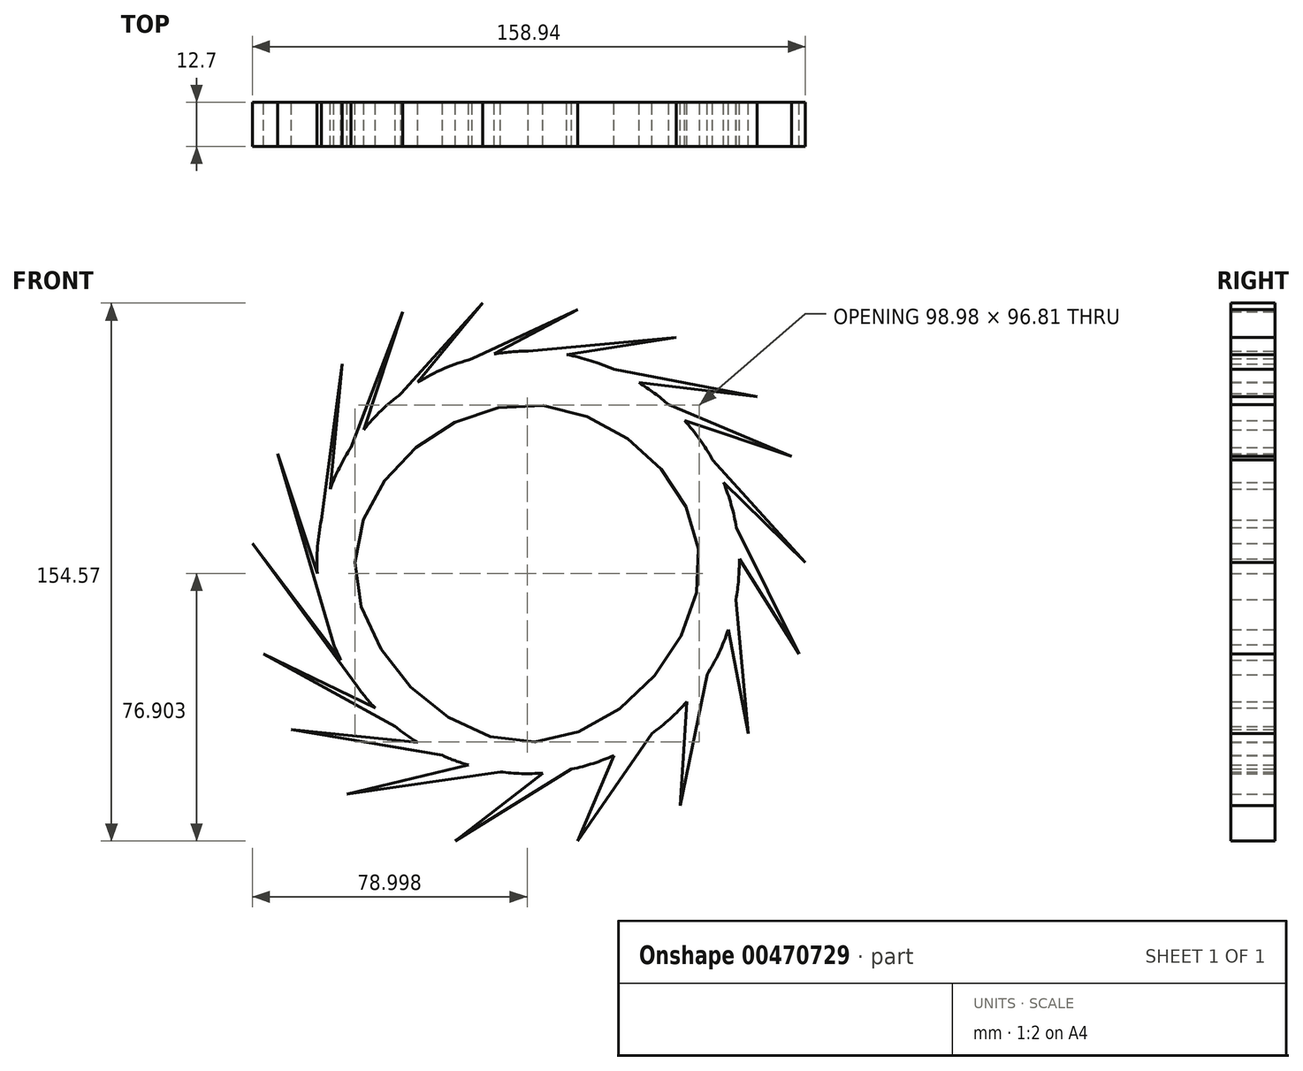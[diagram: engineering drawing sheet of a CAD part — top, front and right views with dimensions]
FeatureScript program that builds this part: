
annotation { "Feature Type Name" : "Feature", "Feature Type Description" : "" }
export const myFeature = defineFeature(function(context is Context, id is Id, definition is map)
    precondition{}
    {
        {
            var Q0;
            Q0=qCreatedBy(makeId("Front.planeOp"),FACE);
            var sketch = newSketch(context, id + "F0", { "sketchPlane" : qUnion([Q0])});
            skArc(sketch, "E0", {"start": v(-16.12, 58.5) * mm, "mid": v(-24.14, 55.68) * mm, "end": v(-31.68, 51.76) * mm});
            skLineSegment(sketch, "E1", {"start": v(-59.45, 12.2) * mm, "end": v(-53.45, 57.05) * mm});
            skLineSegment(sketch, "E2", {"start": v(-53.45, 57.05) * mm, "end": v(-56.92, 21.05) * mm});
            skLineSegment(sketch, "E3", {"start": v(-50.89, 33.06) * mm, "end": v(-36, 71.96) * mm});
            skLineSegment(sketch, "E4", {"start": v(-36, 71.96) * mm, "end": v(-47.22, 38.12) * mm});
            skLineSegment(sketch, "E5", {"start": v(-36.49, 48.5) * mm, "end": v(-13.08, 74.5) * mm});
            skLineSegment(sketch, "E6", {"start": v(-13.08, 74.5) * mm, "end": v(-31.68, 51.76) * mm});
            skLineSegment(sketch, "E7", {"start": v(-16.12, 58.5) * mm, "end": v(14.2, 72.69) * mm});
            skLineSegment(sketch, "E8", {"start": v(14.2, 72.69) * mm, "end": v(-9.8, 59.9) * mm});
            skArc(sketch, "E9.trimOffspring", {"start": v(-36.49, 48.5) * mm, "mid": v(-42.17, 43.64) * mm, "end": v(-47.22, 38.12) * mm});
            skArc(sketch, "E10.trimOffspring", {"start": v(-50.89, 33.06) * mm, "mid": v(-54.24, 27.23) * mm, "end": v(-56.92, 21.05) * mm});
            skArc(sketch, "E11.trimOffspring", {"start": v(-59.45, 12.2) * mm, "mid": v(-60.51, 4.55) * mm, "end": v(-60.6, -3.17) * mm});
            skArc(sketch, "E12.trimOffspring", {"start": v(-55.87, -23.69) * mm, "mid": v(-54.89, -25.89) * mm, "end": v(-53.82, -28.04) * mm});
            skLineSegment(sketch, "E13", {"start": v(0, 60.69) * mm, "end": v(42.56, 64.68) * mm});
            skLineSegment(sketch, "E14", {"start": v(42.56, 64.68) * mm, "end": v(11.13, 59.66) * mm});
            skLineSegment(sketch, "E15", {"start": v(24.64, 55.46) * mm, "end": v(65.84, 47.6) * mm});
            skLineSegment(sketch, "E16", {"start": v(65.84, 47.6) * mm, "end": v(31.86, 51.65) * mm});
            skLineSegment(sketch, "E17", {"start": v(40.42, 45.27) * mm, "end": v(75.66, 30.5) * mm});
            skLineSegment(sketch, "E18", {"start": v(75.66, 30.5) * mm, "end": v(44.98, 40.74) * mm});
            skLineSegment(sketch, "E19", {"start": v(53.04, 29.48) * mm, "end": v(79.66, 0) * mm});
            skLineSegment(sketch, "E20", {"start": v(79.66, 0) * mm, "end": v(56.18, 22.95) * mm});
            skArc(sketch, "E21.trimOffspring", {"start": v(24.64, 55.46) * mm, "mid": v(18, 57.95) * mm, "end": v(11.13, 59.66) * mm});
            skArc(sketch, "E22.trimOffspring", {"start": v(0, 60.69) * mm, "mid": v(-4.91, 60.49) * mm, "end": v(-9.8, 59.9) * mm});
            skArc(sketch, "E23.trimOffspring", {"start": v(40.42, 45.27) * mm, "mid": v(36.28, 48.65) * mm, "end": v(31.86, 51.65) * mm});
            skArc(sketch, "E24.trimOffspring", {"start": v(53.04, 29.48) * mm, "mid": v(49.33, 35.34) * mm, "end": v(44.98, 40.74) * mm});
            skLineSegment(sketch, "E25", {"start": v(59.74, -10.68) * mm, "end": v(63.3, -49.16) * mm});
            skLineSegment(sketch, "E26", {"start": v(63.3, -49.16) * mm, "end": v(57.52, -19.33) * mm});
            skArc(sketch, "E27.trimOffspring", {"start": v(59.86, 9.96) * mm, "mid": v(58.38, 16.56) * mm, "end": v(56.18, 22.95) * mm});
            skArc(sketch, "E28.trimOffspring", {"start": v(59.74, -10.68) * mm, "mid": v(60.49, -4.88) * mm, "end": v(60.68, 0.96) * mm});
            skLineSegment(sketch, "E29", {"start": v(51.43, -32.2) * mm, "end": v(43.66, -69.89) * mm});
            skLineSegment(sketch, "E30", {"start": v(43.66, -69.89) * mm, "end": v(45.58, -40.06) * mm});
            skArc(sketch, "E31.trimOffspring", {"start": v(51.43, -32.2) * mm, "mid": v(54.86, -25.95) * mm, "end": v(57.52, -19.33) * mm});
            skLineSegment(sketch, "E32", {"start": v(-60.6, -3.17) * mm, "end": v(-72, 31.22) * mm});
            skLineSegment(sketch, "E33", {"start": v(-72, 31.22) * mm, "end": v(-55.87, -23.69) * mm});
            skLineSegment(sketch, "E34", {"start": v(60.68, 0.96) * mm, "end": v(77.84, -26.24) * mm});
            skLineSegment(sketch, "E35", {"start": v(77.84, -26.24) * mm, "end": v(59.86, 9.96) * mm});
            skLineSegment(sketch, "E36", {"start": v(35.53, -49.2) * mm, "end": v(14.2, -80.07) * mm});
            skLineSegment(sketch, "E37", {"start": v(14.2, -80.07) * mm, "end": v(24.61, -55.47) * mm});
            skArc(sketch, "E38.trimOffspring", {"start": v(35.53, -49.2) * mm, "mid": v(40.81, -44.91) * mm, "end": v(45.58, -40.06) * mm});
            skLineSegment(sketch, "E39", {"start": v(12.52, -59.38) * mm, "end": v(-20.98, -80.07) * mm});
            skLineSegment(sketch, "E40", {"start": v(-20.98, -80.07) * mm, "end": v(4.26, -60.54) * mm});
            skArc(sketch, "E41.trimOffspring", {"start": v(12.52, -59.38) * mm, "mid": v(18.67, -57.74) * mm, "end": v(24.61, -55.47) * mm});
            skLineSegment(sketch, "E42", {"start": v(-7.91, -60.17) * mm, "end": v(-52, -66.61) * mm});
            skLineSegment(sketch, "E43", {"start": v(-52, -66.61) * mm, "end": v(-17.17, -58.2) * mm});
            skLineSegment(sketch, "E44", {"start": v(-24.67, -55.45) * mm, "end": v(-68, -48.06) * mm});
            skLineSegment(sketch, "E45", {"start": v(-68, -48.06) * mm, "end": v(-31.7, -51.74) * mm});
            skLineSegment(sketch, "E46", {"start": v(-38.23, -47.13) * mm, "end": v(-76, -26.24) * mm});
            skLineSegment(sketch, "E47", {"start": v(-76, -26.24) * mm, "end": v(-43.95, -41.84) * mm});
            skLineSegment(sketch, "E48", {"start": v(-48.65, -36.27) * mm, "end": v(-79.28, 5.4) * mm});
            skLineSegment(sketch, "E49", {"start": v(-79.28, 5.4) * mm, "end": v(-53.82, -28.04) * mm});
            skArc(sketch, "E50.trimOffspring", {"start": v(-7.91, -60.17) * mm, "mid": v(-1.83, -60.66) * mm, "end": v(4.26, -60.54) * mm});
            skArc(sketch, "E51.trimOffspring", {"start": v(-24.67, -55.45) * mm, "mid": v(-20.96, -56.95) * mm, "end": v(-17.17, -58.2) * mm});
            skArc(sketch, "E52.trimOffspring", {"start": v(-38.23, -47.13) * mm, "mid": v(-35.04, -49.54) * mm, "end": v(-31.7, -51.74) * mm});
            skArc(sketch, "E53.trimOffspring", {"start": v(-49.15, -35.6) * mm, "mid": v(-46.65, -38.8) * mm, "end": v(-43.95, -41.84) * mm});
            skSolve(sketch);
        }
        {
            var Q0;
            Q0 = qSketchRegion(id + "F0", true);
            extrude(context, id + "F1", {"entities" : qUnion([Q0]), "depth" : 12.7 * mm});
        }
        {
            var Q0;
            Q0=makeQuery(id+"F1.opExtrude","CAP_FACE",FACE,{"disambiguationData":[OSD([sQuery(id+"F0.wireOp",EDGE,"E0"),sQuery(id+"F0.wireOp",EDGE,"E1"),sQuery(id+"F0.wireOp",EDGE,"E2"),sQuery(id+"F0.wireOp",EDGE,"E3"),sQuery(id+"F0.wireOp",EDGE,"E4"),sQuery(id+"F0.wireOp",EDGE,"E5"),sQuery(id+"F0.wireOp",EDGE,"E6"),sQuery(id+"F0.wireOp",EDGE,"E7"),sQuery(id+"F0.wireOp",EDGE,"E8"),sQuery(id+"F0.wireOp",EDGE,"E9.trimOffspring"),sQuery(id+"F0.wireOp",EDGE,"E10.trimOffspring"),sQuery(id+"F0.wireOp",EDGE,"E11.trimOffspring"),sQuery(id+"F0.wireOp",EDGE,"E12.trimOffspring"),sQuery(id+"F0.wireOp",EDGE,"E13"),sQuery(id+"F0.wireOp",EDGE,"E14"),sQuery(id+"F0.wireOp",EDGE,"E15"),sQuery(id+"F0.wireOp",EDGE,"E16"),sQuery(id+"F0.wireOp",EDGE,"E17"),sQuery(id+"F0.wireOp",EDGE,"E18"),sQuery(id+"F0.wireOp",EDGE,"E19"),sQuery(id+"F0.wireOp",EDGE,"E20"),sQuery(id+"F0.wireOp",EDGE,"E21.trimOffspring"),sQuery(id+"F0.wireOp",EDGE,"E22.trimOffspring"),sQuery(id+"F0.wireOp",EDGE,"E23.trimOffspring"),sQuery(id+"F0.wireOp",EDGE,"E24.trimOffspring"),sQuery(id+"F0.wireOp",EDGE,"E25"),sQuery(id+"F0.wireOp",EDGE,"E26"),sQuery(id+"F0.wireOp",EDGE,"E27.trimOffspring"),sQuery(id+"F0.wireOp",EDGE,"E28.trimOffspring"),sQuery(id+"F0.wireOp",EDGE,"E29"),sQuery(id+"F0.wireOp",EDGE,"E30"),sQuery(id+"F0.wireOp",EDGE,"E31.trimOffspring"),sQuery(id+"F0.wireOp",EDGE,"E32"),sQuery(id+"F0.wireOp",EDGE,"E33"),sQuery(id+"F0.wireOp",EDGE,"E34"),sQuery(id+"F0.wireOp",EDGE,"E35"),sQuery(id+"F0.wireOp",EDGE,"E36"),sQuery(id+"F0.wireOp",EDGE,"E37"),sQuery(id+"F0.wireOp",EDGE,"E38.trimOffspring"),sQuery(id+"F0.wireOp",EDGE,"E39"),sQuery(id+"F0.wireOp",EDGE,"E40"),sQuery(id+"F0.wireOp",EDGE,"E41.trimOffspring"),sQuery(id+"F0.wireOp",EDGE,"E42"),sQuery(id+"F0.wireOp",EDGE,"E43"),sQuery(id+"F0.wireOp",EDGE,"E44"),sQuery(id+"F0.wireOp",EDGE,"E45"),sQuery(id+"F0.wireOp",EDGE,"E46"),sQuery(id+"F0.wireOp",EDGE,"E47"),sQuery(id+"F0.wireOp",EDGE,"E48"),sQuery(id+"F0.wireOp",EDGE,"E49"),sQuery(id+"F0.wireOp",EDGE,"E50.trimOffspring"),sQuery(id+"F0.wireOp",EDGE,"E51.trimOffspring"),sQuery(id+"F0.wireOp",EDGE,"E52.trimOffspring"),sQuery(id+"F0.wireOp",EDGE,"E53.trimOffspring")])],"isStart":false});
            var sketch = newSketch(context, id + "F2", { "sketchPlane" : qUnion([Q0])});
            skPoint(sketch, "E54.MirrorCS.center.orphan", {"position": v(0, 0) * mm});
            skFitSpline(sketch, "E55", {"points": [v(-49.77, 0) * mm, v(0, 45.25) * mm, v(49.23, 0) * mm, v(0, -51.6) * mm, v(-49.77, 0) * mm]});
            skSolve(sketch);
        }
        {
            var Q0;
            Q0 = qSketchRegion(id + "F2", true);
            extrude(context, id + "F3", {"entities" : qUnion([Q0]), "operationType" : NewBodyOperationType.REMOVE, "oppositeDirection" : true, "depth" : 25.4 * mm});
        }
    });
